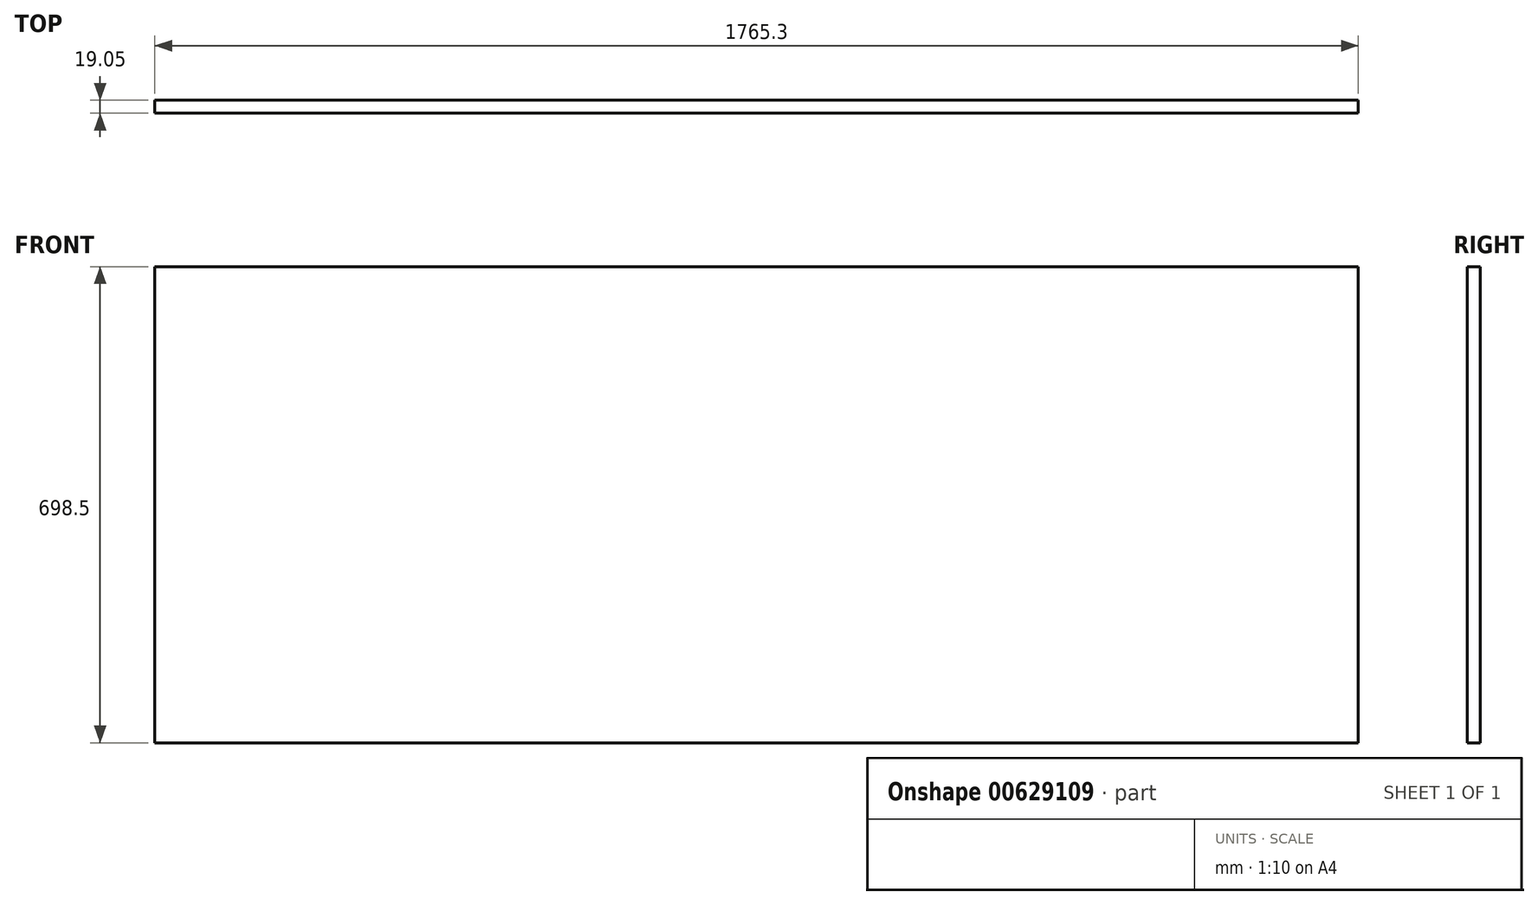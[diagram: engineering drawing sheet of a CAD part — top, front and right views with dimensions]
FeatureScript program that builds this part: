
annotation { "Feature Type Name" : "Feature", "Feature Type Description" : "" }
export const myFeature = defineFeature(function(context is Context, id is Id, definition is map)
    precondition{}
    {
        {
            var Q0;
            Q0=qCreatedBy(makeId("Front.planeOp"),FACE);
            var sketch = newSketch(context, id + "F0", { "sketchPlane" : qUnion([Q0])});
            skLineSegment(sketch, "E0.bottom", {"start": v(-882.65, 349.25) * mm, "end": v(882.65, 349.25) * mm});
            skLineSegment(sketch, "E0.top", {"start": v(-882.65, -349.25) * mm, "end": v(882.65, -349.25) * mm});
            skLineSegment(sketch, "E0.left", {"start": v(-882.65, 349.25) * mm, "end": v(-882.65, -349.25) * mm});
            skLineSegment(sketch, "E0.right", {"start": v(882.65, 349.25) * mm, "end": v(882.65, -349.25) * mm});
            skPoint(sketch, "E0.middle", {"position": v(0, 0) * mm});
            skSolve(sketch);
        }
        {
            var Q0;
            Q0=makeQuery(id+"F0.imprint","IMPRINT",FACE,{"disambiguationData":[TD([[makeQuery(id+"F0.imprint","IMPRINT",EDGE,{"derivedFrom":sQuery(id+"F0.wireOp",EDGE,"E0.bottom")}),-1.0]])]});
            extrude(context, id + "F1", {"entities" : qUnion([Q0]), "depth" : 19.05 * mm, "offsetDistance" : 25.4 * mm});
        }
    });
